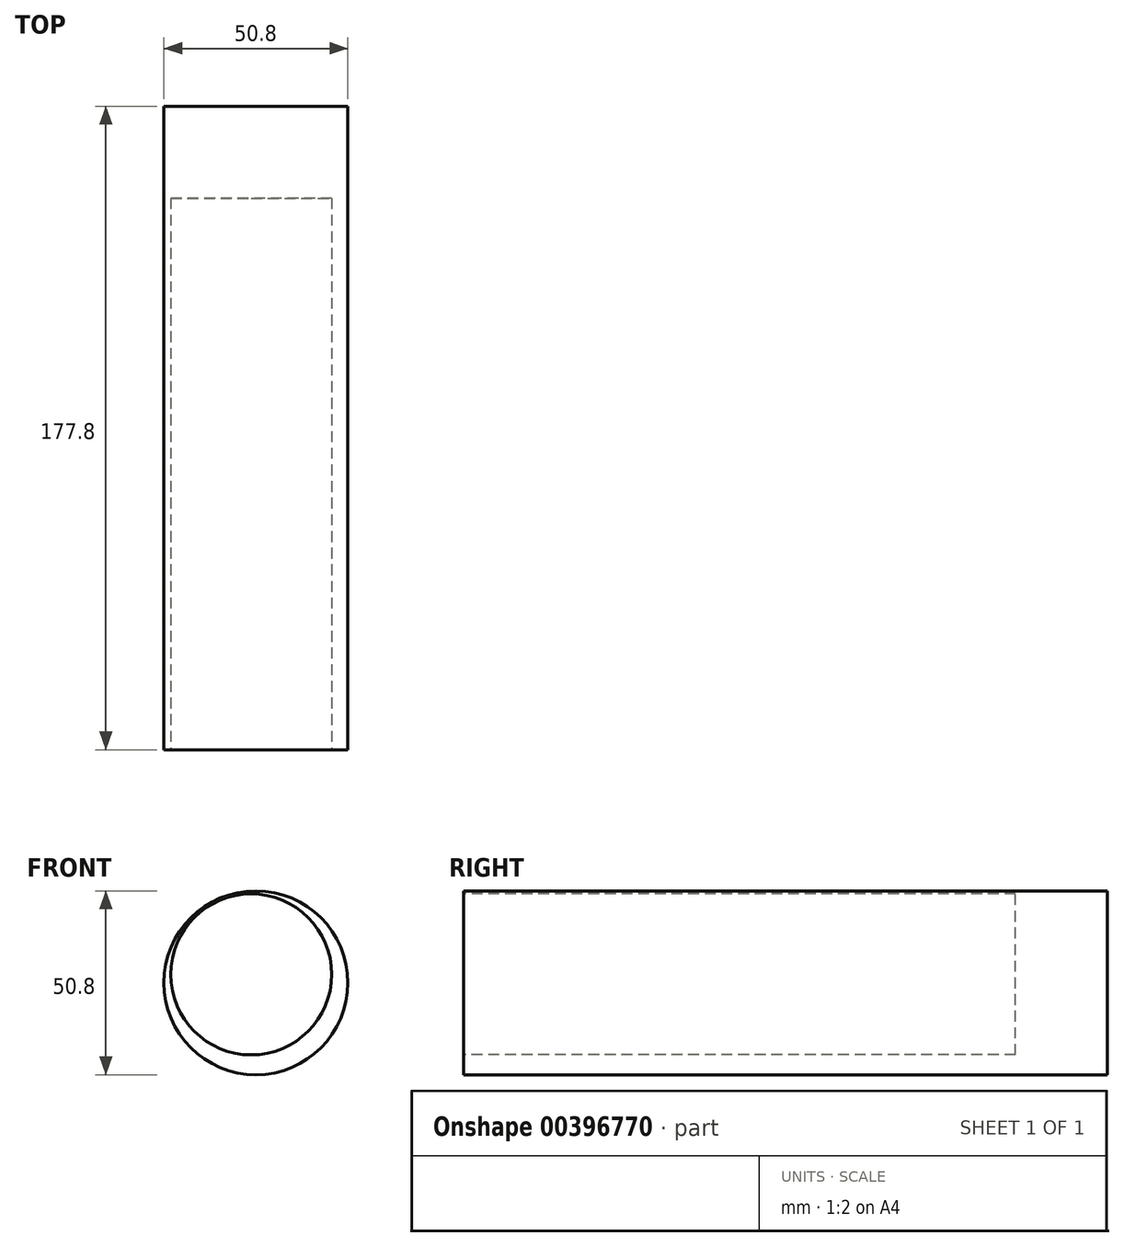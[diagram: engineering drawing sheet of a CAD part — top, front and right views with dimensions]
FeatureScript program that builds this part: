
annotation { "Feature Type Name" : "Feature", "Feature Type Description" : "" }
export const myFeature = defineFeature(function(context is Context, id is Id, definition is map)
    precondition{}
    {
        {
            var Q0;
            Q0=qCreatedBy(makeId("Front.planeOp"),FACE);
            var sketch = newSketch(context, id + "F0", { "sketchPlane" : qUnion([Q0])});
            skCircle(sketch, "E0", {"center": v(0, 0) * mm, "radius": 25.4 * mm});
            skSolve(sketch);
        }
        {
            var Q0;
            Q0 = qSketchRegion(id + "F0", true);
            extrude(context, id + "F1", {"entities" : qUnion([Q0]), "depth" : 152.4 * mm});
        }
        {
            var Q0;
            Q0=makeQuery(id+"F1.opExtrude","CAP_FACE",FACE,{"disambiguationData":[OSD([sQuery(id+"F0.wireOp",EDGE,"E0")])],"isStart":false});
            var sketch = newSketch(context, id + "F2", { "sketchPlane" : qUnion([Q0])});
            skCircle(sketch, "E1", {"center": v(-1.28, 2.3) * mm, "radius": 22.23 * mm});
            skSolve(sketch);
        }
        {
            var Q0;
            Q0 = qSketchRegion(id + "F2", true);
            extrude(context, id + "F3", {"entities" : qUnion([Q0]), "operationType" : NewBodyOperationType.REMOVE, "oppositeDirection" : true, "depth" : 146.05 * mm});
        }
        {
            var Q0;
            Q0=makeQuery(id+"F1.opExtrude","CAP_FACE",FACE,{"disambiguationData":[OSD([sQuery(id+"F0.wireOp",EDGE,"E0")])],"isStart":false});
            var Q1;
            Q1=makeQuery(id+"F1.opExtrude","CAP_FACE",FACE,{"disambiguationData":[OSD([sQuery(id+"F0.wireOp",EDGE,"E0")])],"isStart":true});
            extrude(context, id + "F4", {"entities" : qUnion([Q0, Q1]), "operationType" : NewBodyOperationType.ADD, "depth" : 25.4 * mm});
        }
    });
